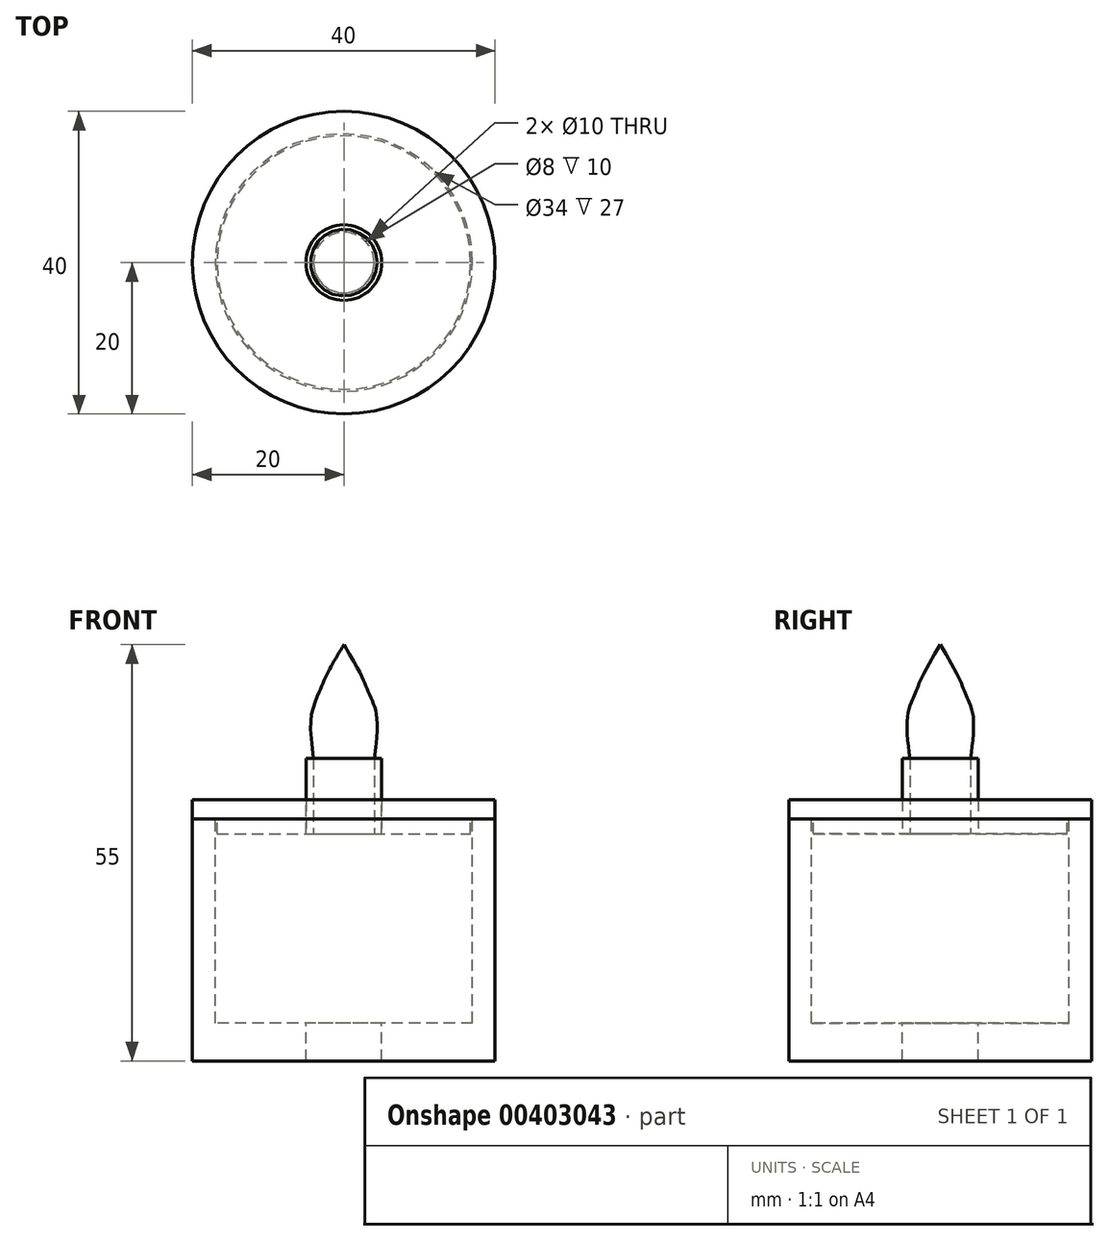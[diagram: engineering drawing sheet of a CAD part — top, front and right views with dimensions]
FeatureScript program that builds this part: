
annotation { "Feature Type Name" : "Feature", "Feature Type Description" : "" }
export const myFeature = defineFeature(function(context is Context, id is Id, definition is map)
    precondition{}
    {
        {
            var Q0;
            Q0=qCreatedBy(makeId("Top.planeOp"),FACE);
            var sketch = newSketch(context, id + "F0", { "sketchPlane" : qUnion([Q0])});
            skCircle(sketch, "E0", {"center": v(0, 0) * mm, "radius": 20 * mm});
            skSolve(sketch);
        }
        {
            var Q0;
            Q0 = qSketchRegion(id + "F0", true);
            extrude(context, id + "F1", {"entities" : qUnion([Q0]), "depth" : 32 * mm});
        }
        {
            var Q0;
            Q0=makeQuery(id+"F1.opExtrude","CAP_FACE",FACE,{"disambiguationData":[OSD([sQuery(id+"F0.wireOp",EDGE,"E0")])],"isStart":false});
            var sketch = newSketch(context, id + "F2", { "sketchPlane" : qUnion([Q0])});
            skCircle(sketch, "E1", {"center": v(0, 0) * mm, "radius": 17 * mm});
            skSolve(sketch);
        }
        {
            var Q0;
            Q0 = qSketchRegion(id + "F2", true);
            extrude(context, id + "F3", {"entities" : qUnion([Q0]), "operationType" : NewBodyOperationType.REMOVE, "oppositeDirection" : true, "depth" : 27 * mm});
        }
        {
            var Q0;
            Q0=makeQuery(id+"F1.opExtrude","CAP_FACE",FACE,{"disambiguationData":[OSD([sQuery(id+"F0.wireOp",EDGE,"E0")])],"isStart":false});
            var sketch = newSketch(context, id + "F4", { "sketchPlane" : qUnion([Q0])});
            skCircle(sketch, "E2.0", {"center": v(0, 0) * mm, "radius": 20 * mm});
            skSolve(sketch);
        }
        {
            var Q0;
            Q0 = qSketchRegion(id + "F4", true);
            extrude(context, id + "F5", {"entities" : qUnion([Q0]), "depth" : 2.5 * mm});
        }
        {
            var Q0;
            Q0=makeQuery(id+"F5.opExtrude","CAP_FACE",FACE,{"disambiguationData":[OSD([sQuery(id+"F4.wireOp",EDGE,"E2.0")])],"isStart":true});
            var sketch = newSketch(context, id + "F6", { "sketchPlane" : qUnion([Q0])});
            skCircle(sketch, "E3", {"center": v(0, 0) * mm, "radius": 16.75 * mm});
            skSolve(sketch);
        }
        {
            var Q0;
            Q0 = qSketchRegion(id + "F6", true);
            extrude(context, id + "F7", {"entities" : qUnion([Q0]), "operationType" : NewBodyOperationType.ADD, "depth" : 2 * mm});
        }
        {
            var Q0;
            Q0=makeQuery(id+"F5.opExtrude","CAP_FACE",FACE,{"disambiguationData":[OSD([sQuery(id+"F4.wireOp",EDGE,"E2.0")])],"isStart":false});
            var sketch = newSketch(context, id + "F8", { "sketchPlane" : qUnion([Q0])});
            skCircle(sketch, "E4", {"center": v(0, 0) * mm, "radius": 5 * mm});
            skSolve(sketch);
        }
        {
            var Q0;
            Q0 = qSketchRegion(id + "F8", true);
            extrude(context, id + "F9", {"entities" : qUnion([Q0]), "operationType" : NewBodyOperationType.REMOVE, "endBound" : BoundingType.THROUGH_ALL, "oppositeDirection" : true, "depth" : 25 * mm});
        }
        {
            var Q0;
            Q0=makeQuery(id+"F7.opExtrude","CAP_FACE",FACE,{"disambiguationData":[OSD([sQuery(id+"F6.wireOp",EDGE,"E3")])],"isStart":false});
            var sketch = newSketch(context, id + "F10", { "sketchPlane" : qUnion([Q0])});
            skCircle(sketch, "E5.0", {"center": v(0, 0) * mm, "radius": 5 * mm});
            skCircle(sketch, "E6", {"center": v(0, 0) * mm, "radius": 4 * mm});
            skSolve(sketch);
        }
        {
            var Q0;
            Q0 = qSketchRegion(id + "F10", true);
            extrude(context, id + "F11", {"entities" : qUnion([Q0]), "oppositeDirection" : true, "depth" : 10 * mm});
        }
        {
            var Q0;
            Q0=qCreatedBy(makeId("Front.planeOp"),FACE);
            var sketch = newSketch(context, id + "F12", { "sketchPlane" : qUnion([Q0])});
            skLineSegment(sketch, "E7.0", {"start": v(4, 40) * mm, "end": v(0, 40) * mm});
            skLineSegment(sketch, "E8", {"start": v(0, 40) * mm, "end": v(0, 55) * mm});
            skPoint(sketch, "E8.endSnap0", {"position": v(0, 40) * mm});
            skFitSpline(sketch, "E9", {"points": [v(4, 40) * mm, v(3.88, 47.26) * mm, v(3, 49.36) * mm, v(0, 55) * mm], "startDerivative": vector(5.26, 36.55) * mm, "endDerivative": vector(-18.61, 30.5) * mm});
            skLineSegment(sketch, "E10.0", {"start": v(4, 40) * mm, "end": v(-4, 40) * mm});
            skSolve(sketch);
        }
        {
            var Q0;
            Q0 = qSketchRegion(id + "F12", true);
            var Q1;
            Q1=sQuery(id+"F12.wireOp",EDGE,"E8");
            revolve(context, id + "F13", {"entities" : qUnion([Q0]), "axis" : qUnion([Q1]), "revolveType" : RevolveType.FULL});
        }
    });
